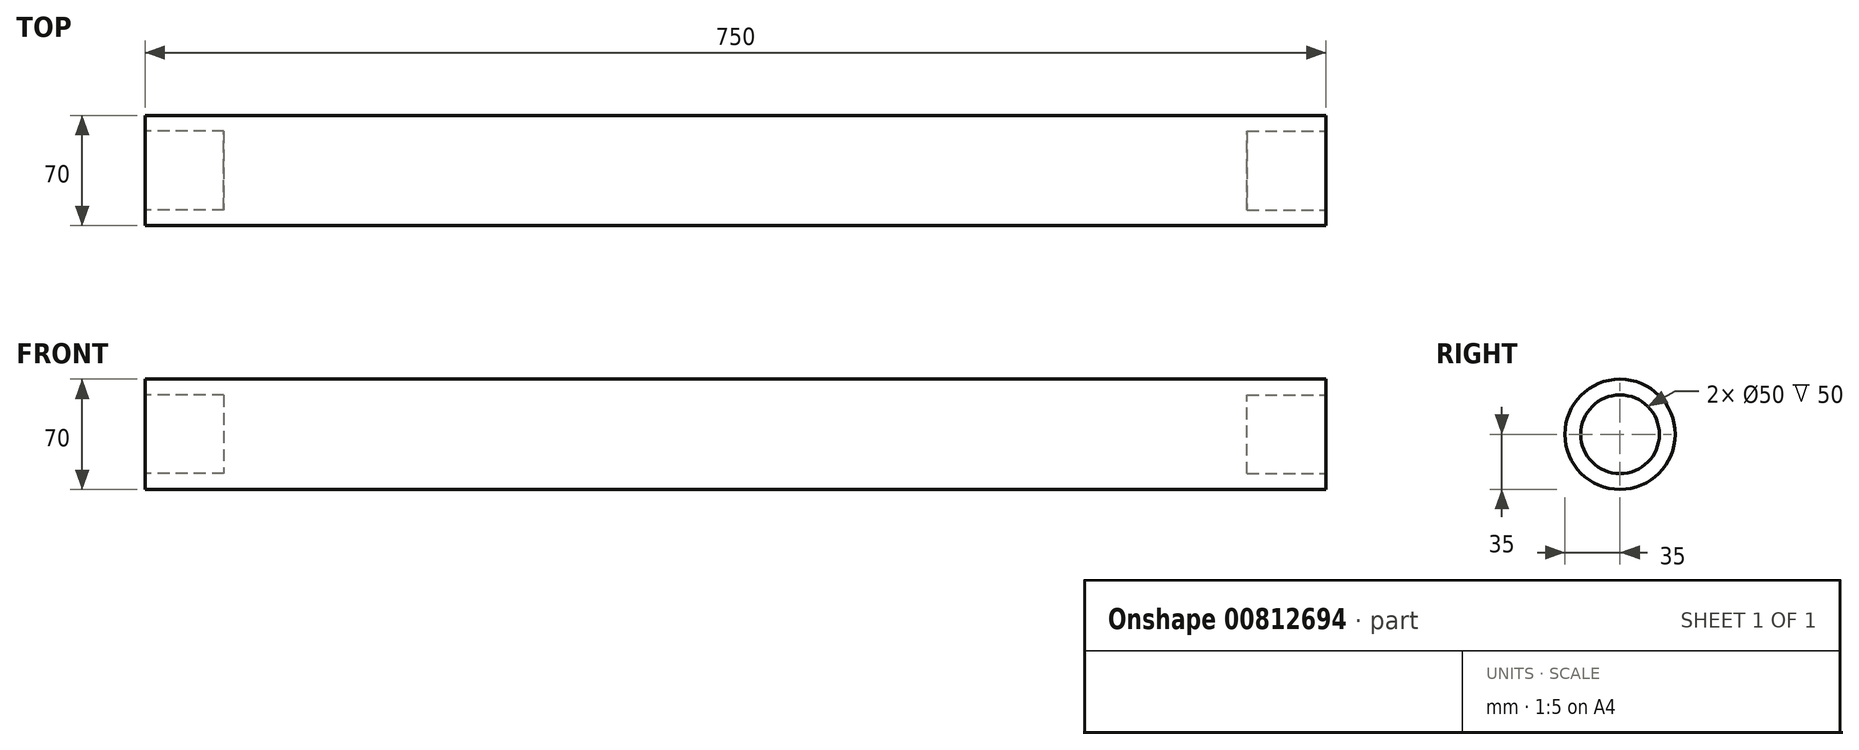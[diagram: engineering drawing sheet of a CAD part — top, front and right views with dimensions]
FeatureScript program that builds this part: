
annotation { "Feature Type Name" : "Feature", "Feature Type Description" : "" }
export const myFeature = defineFeature(function(context is Context, id is Id, definition is map)
    precondition{}
    {
        {
            var Q0;
            Q0=qCreatedBy(makeId("Right.planeOp"),FACE);
            var sketch = newSketch(context, id + "F0", { "sketchPlane" : qUnion([Q0])});
            skCircle(sketch, "E0", {"center": v(0, 0) * mm, "radius": 35 * mm});
            skSolve(sketch);
        }
        {
            var Q0;
            Q0=makeQuery(id+"F0.imprint","IMPRINT",FACE,{"disambiguationData":[TD([[makeQuery(id+"F0.imprint","IMPRINT",EDGE,{"derivedFrom":sQuery(id+"F0.wireOp",EDGE,"E0")}),1.0]])]});
            extrude(context, id + "F1", {"entities" : qUnion([Q0]), "endBound" : BoundingType.SYMMETRIC, "depth" : 750 * mm, "offsetDistance" : 25 * mm});
        }
        {
            var Q0;
            Q0=makeQuery(id+"F1.opExtrude","CAP_FACE",FACE,{"disambiguationData":[OSD([sQuery(id+"F0.wireOp",EDGE,"E0")])],"isStart":false});
            var sketch = newSketch(context, id + "F2", { "sketchPlane" : qUnion([Q0])});
            skCircle(sketch, "E1", {"center": v(0, 0) * mm, "radius": 25 * mm});
            skSolve(sketch);
        }
        {
            var Q0;
            Q0 = qSketchRegion(id + "F2", true);
            extrude(context, id + "F3", {"entities" : qUnion([Q0]), "operationType" : NewBodyOperationType.REMOVE, "oppositeDirection" : true, "depth" : 50 * mm, "offsetDistance" : 25 * mm});
        }
        {
            var Q0;
            Q0=makeQuery(id+"F1.opExtrude","CAP_FACE",FACE,{"disambiguationData":[OSD([sQuery(id+"F0.wireOp",EDGE,"E0")])],"isStart":true});
            var sketch = newSketch(context, id + "F4", { "sketchPlane" : qUnion([Q0])});
            skCircle(sketch, "E2", {"center": v(0, 0) * mm, "radius": 25 * mm});
            skSolve(sketch);
        }
        {
            var Q0;
            Q0 = qSketchRegion(id + "F4", true);
            extrude(context, id + "F5", {"entities" : qUnion([Q0]), "operationType" : NewBodyOperationType.REMOVE, "oppositeDirection" : true, "depth" : 50 * mm, "offsetDistance" : 25 * mm});
        }
    });
